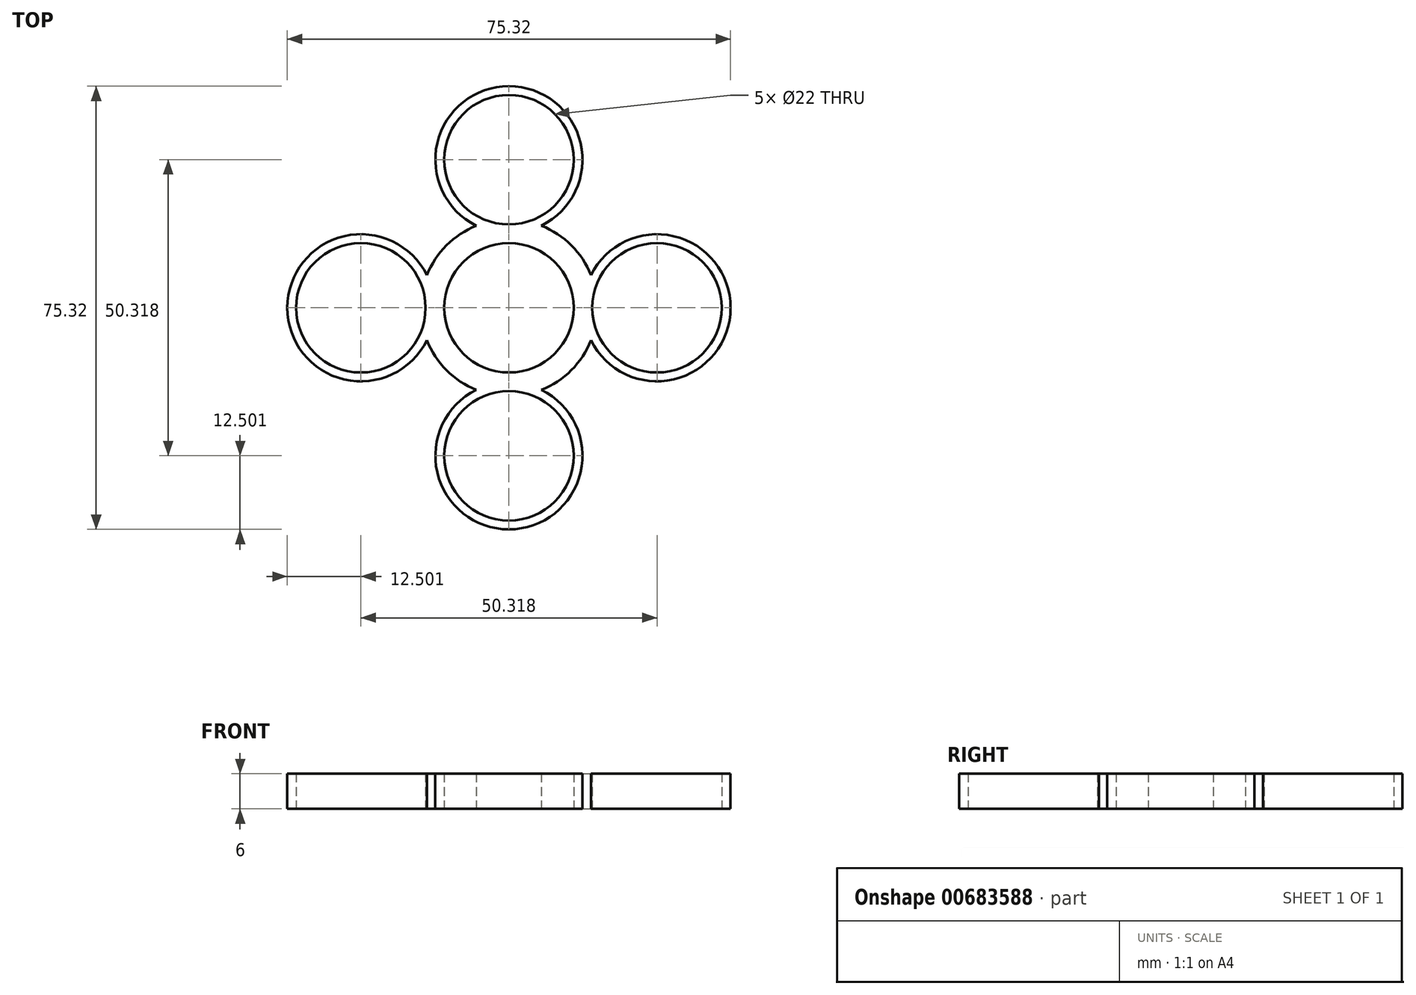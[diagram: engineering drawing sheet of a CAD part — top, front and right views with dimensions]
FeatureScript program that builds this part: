
annotation { "Feature Type Name" : "Feature", "Feature Type Description" : "" }
export const myFeature = defineFeature(function(context is Context, id is Id, definition is map)
    precondition{}
    {
        {
            var Q0;
            Q0=qCreatedBy(makeId("Top.planeOp"),FACE);
            var sketch = newSketch(context, id + "F0", { "sketchPlane" : qUnion([Q0])});
            skArc(sketch, "E0", {"start": v(7.78, 7.78) * mm, "mid": v(0, 11) * mm, "end": v(-7.78, 7.78) * mm});
            skArc(sketch, "E1", {"start": v(-5.52, 13.95) * mm, "mid": v(-8.24, 12.54) * mm, "end": v(-10.6, 10.6) * mm});
            skCircle(sketch, "E2", {"center": v(0, 25.16) * mm, "radius": 11 * mm});
            skArc(sketch, "E3", {"start": v(5.52, 13.95) * mm, "mid": v(0, 37.66) * mm, "end": v(-5.52, 13.95) * mm});
            skLineSegment(sketch, "E4", {"start": v(-15, 0) * mm, "end": v(15, 0) * mm});
            skArc(sketch, "E5.trimOffspring", {"start": v(10.6, 10.6) * mm, "mid": v(8.24, 12.54) * mm, "end": v(5.52, 13.95) * mm});
            skPoint(sketch, "E6.center.orphan", {"position": v(-24.74, 0) * mm});
            skPoint(sketch, "E7.MirrorCS.end.orphan", {"position": v(-15, 0) * mm});
            skPoint(sketch, "E7.MirrorCS.start.orphan", {"position": v(-5.52, -13.95) * mm});
            skPoint(sketch, "E8.MirrorCS.end.orphan", {"position": v(-11, 0) * mm});
            skPoint(sketch, "E8.MirrorCS.start.orphan", {"position": v(11, 0) * mm});
            skPoint(sketch, "E9.MirrorCS.end.orphan", {"position": v(5.52, -13.95) * mm});
            skPoint(sketch, "E9.MirrorCS.start.orphan", {"position": v(15, 0) * mm});
            skArc(sketch, "E10.1.0", {"start": v(-7.78, 7.78) * mm, "mid": v(-11, 0) * mm, "end": v(-7.78, -7.78) * mm});
            skArc(sketch, "E10.1.1", {"start": v(-13.95, 5.52) * mm, "mid": v(-37.66, 0) * mm, "end": v(-13.95, -5.52) * mm});
            skCircle(sketch, "E10.1.2", {"center": v(-25.16, 0) * mm, "radius": 11 * mm});
            skArc(sketch, "E10.1.3", {"start": v(-10.6, 10.6) * mm, "mid": v(-12.54, 8.24) * mm, "end": v(-13.95, 5.52) * mm});
            skArc(sketch, "E10.1.4", {"start": v(-13.95, -5.52) * mm, "mid": v(-12.54, -8.24) * mm, "end": v(-10.6, -10.6) * mm});
            skArc(sketch, "E10.2.0", {"start": v(-7.78, -7.78) * mm, "mid": v(0, -11) * mm, "end": v(7.78, -7.78) * mm});
            skArc(sketch, "E10.2.1", {"start": v(-5.52, -13.95) * mm, "mid": v(0, -37.66) * mm, "end": v(5.52, -13.95) * mm});
            skCircle(sketch, "E10.2.2", {"center": v(0, -25.16) * mm, "radius": 11 * mm});
            skArc(sketch, "E10.2.3", {"start": v(-10.6, -10.6) * mm, "mid": v(-8.24, -12.54) * mm, "end": v(-5.52, -13.95) * mm});
            skArc(sketch, "E10.2.4", {"start": v(5.52, -13.95) * mm, "mid": v(8.24, -12.54) * mm, "end": v(10.6, -10.6) * mm});
            skArc(sketch, "E10.3.0", {"start": v(7.78, -7.78) * mm, "mid": v(11, 0) * mm, "end": v(7.78, 7.78) * mm});
            skArc(sketch, "E10.3.1", {"start": v(13.95, -5.52) * mm, "mid": v(37.66, 0) * mm, "end": v(13.95, 5.52) * mm});
            skCircle(sketch, "E10.3.2", {"center": v(25.16, 0) * mm, "radius": 11 * mm});
            skArc(sketch, "E10.3.3", {"start": v(10.6, -10.6) * mm, "mid": v(12.54, -8.24) * mm, "end": v(13.95, -5.52) * mm});
            skArc(sketch, "E10.3.4", {"start": v(13.95, 5.52) * mm, "mid": v(12.54, 8.24) * mm, "end": v(10.6, 10.6) * mm});
            skSolve(sketch);
        }
        {
            var Q0;
            Q0 = qSketchRegion(id + "F0", true);
            extrude(context, id + "F1", {"entities" : qUnion([Q0]), "depth" : 6 * mm, "offsetDistance" : 25 * mm});
        }
    });
